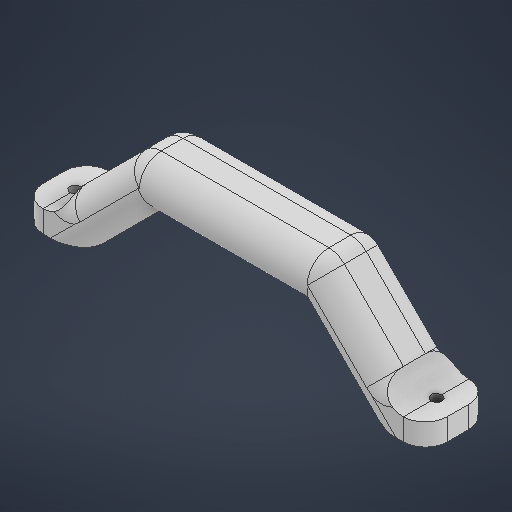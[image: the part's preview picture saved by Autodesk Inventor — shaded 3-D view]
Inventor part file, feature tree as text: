
AUTODESK INVENTOR PART (.ipt)
format: ipt  version: 2025 (Build 290162000, 162)  size: 329,216 bytes
history: native  units: in
note: dims shown in document units (in); Inventor stores cm internally (conversion verified against a paired STEP export)
features: fillet x5, extrude x3, chamfer x3, sketch x2, hole x1
ambient origin geometry x8: Origin, YZ Plane, XZ Plane, XY Plane, X Axis, Y Axis, Z Axis, Center Point
bodies: Solid1 (feature_tree)
feature tree (14):
  sketch  "Sketch1"  dims[d0=7.2874in d1=1.1811in]
  extrude  "Extrusion1"  Depth=7.2874in
  extrude  "Extrusion2"  Depth=0.3937in
  extrude  "Extrusion3"  Depth=0.3937in TaperAngle=0.0deg
  hole  "Hole1"  [1 undecoded]
  fillet  "Fillet1"  Radius=3.937in
  chamfer  "Chamfer1"  Distance=1.1811in
  chamfer  "Chamfer3"  Distance=6.5157in
  chamfer  "Chamfer4"  Distance=0.3937in
  fillet  "Fillet5"  Radius=0.5906in
  fillet  "Fillet6"  Radius=0.5906in
  fillet  "Fillet7"  Radius=1.1811in
  fillet  "Fillet8"  Radius=0.3937in
  sketch  "Sketch2"  dims[d2=6.5in d3=5.7126in d4=0.3937in d5=0.0in d6=1.9685in d7=0.0in d8=3.937in d9=1.1811in d10=0.0in d11=6.5157in d12=0.1936in d13=0.4724in d14=0.1575in d15=0.0787in d16=90.0deg d17=0.315in d18=0.8108in d19=0.3937in d20=0.5906in d21=0.0787in d22=45.0deg d28=0.5906in d29=0.0787in d30=45.0deg d32=1.1811in d33=0.0787in d34=45.0deg d35=0.3937in d36=0.3937in d37=0.3937in d38=0.3937in d23=0.0in d24=0.0in d25=0.0in d26=0.0in d31=0.0in]
note: 1 required parameter value undecoded (feature->parameter linkage not recoverable at this tier; creation-order binding heuristic only, values carry confidence <= 0.55)
